# Revit family: Mac
name_source: partatom
category: Furniture
revit_build: Autodesk Revit 2015 (Build: 20140606_1530(x64)
units: mm (PartAtom-declared; Revit-internal decimal feet)

## types (8) — shared parameters
Manufacturer = Isku Oy
Steel frame material = Steel, chrome
Type Comments = Available as antimicrobial
URL = www.isku.fi

## per-type parameters (varying)
| type | Leg type | Plastic seat | Seat location | Wood seat |
| 3008 Wood seat - low with wheels | cross leg : Cross leg with wheels  h500 | No | 500 mm  [stored 1.64042 ft] | Yes |
| 3008 Wood seat - low with studs | cross leg : Cross leg with stud h500 | No | 500 mm  [stored 1.64042 ft] | Yes |
| 3008 Wood seat - high with wheels | cross leg : Cross leg with wheels  h675 | No | 675 mm  [stored 2.21457 ft] | Yes |
| 3008 Wood seat - high with studs | cross leg : Cross leg with stud h675 | No | 675 mm  [stored 2.21457 ft] | Yes |
| 3008 Composite seat - high with studs | cross leg : Cross leg with stud h675 | Yes | 675 mm  [stored 2.21457 ft] | No |
| 3008 Composite seat - high with wheels | cross leg : Cross leg with wheels  h675 | Yes | 675 mm  [stored 2.21457 ft] | No |
| 3008 Composite seat - low with studs | cross leg : Cross leg with stud h500 | Yes | 500 mm  [stored 1.64042 ft] | No |
| 3008 Composite seat - low with wheels | cross leg : Cross leg with wheels  h500 | Yes | 500 mm  [stored 1.64042 ft] | No |

note: [stored X ft] marks values corroborated as IEEE doubles in the binary element streams (Revit-internal decimal feet)

## geometry (parser evidence)
native form markers: Sweep x63
no freeform markers — native parametric forms only
